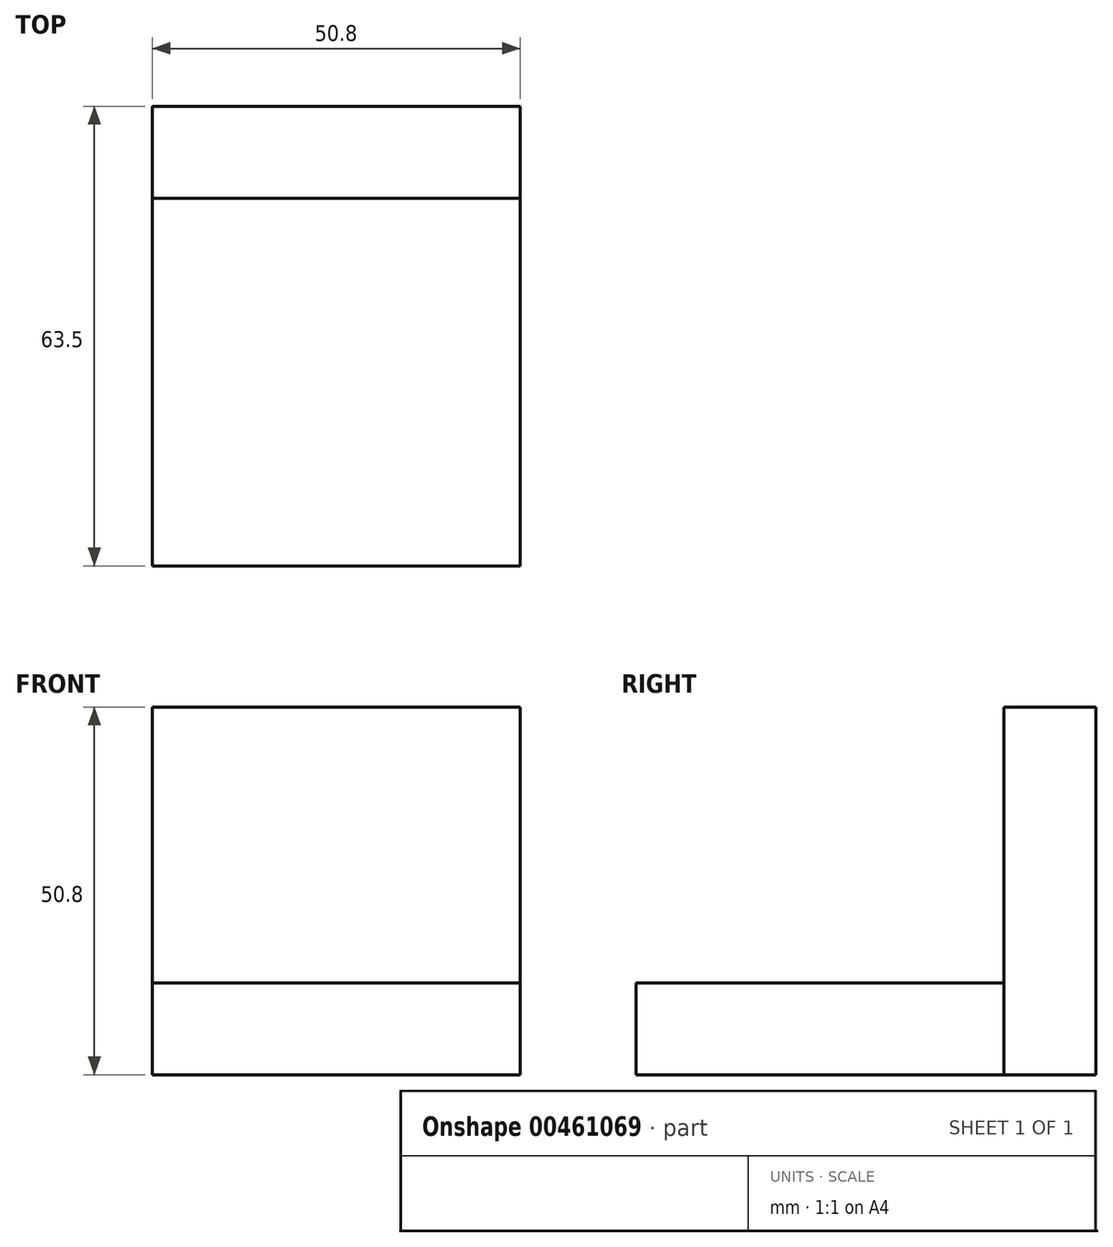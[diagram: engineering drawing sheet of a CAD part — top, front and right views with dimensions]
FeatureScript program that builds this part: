
annotation { "Feature Type Name" : "Feature", "Feature Type Description" : "" }
export const myFeature = defineFeature(function(context is Context, id is Id, definition is map)
    precondition{}
    {
        {
            var Q0;
            Q0=qCreatedBy(makeId("Front.planeOp"),FACE);
            var sketch = newSketch(context, id + "F0", { "sketchPlane" : qUnion([Q0])});
            skLineSegment(sketch, "E0.bottom", {"start": v(-27.86, 37.38) * mm, "end": v(22.94, 37.38) * mm});
            skLineSegment(sketch, "E0.top", {"start": v(-27.86, -13.42) * mm, "end": v(22.94, -13.42) * mm});
            skLineSegment(sketch, "E0.left", {"start": v(-27.86, 37.38) * mm, "end": v(-27.86, -13.42) * mm});
            skLineSegment(sketch, "E0.right", {"start": v(22.94, 37.38) * mm, "end": v(22.94, -13.42) * mm});
            skSolve(sketch);
        }
        {
            var Q0;
            Q0 = qSketchRegion(id + "F0", true);
            extrude(context, id + "F1", {"entities" : qUnion([Q0]), "depth" : 12.7 * mm});
        }
        {
            var Q0;
            Q0=makeQuery(id+"F1.opExtrude","SWEPT_FACE",FACE,{"disambiguationData":[OSD([sQuery(id+"F0.wireOp",EDGE,"E0.top")])]});
            var sketch = newSketch(context, id + "F2", { "sketchPlane" : qUnion([Q0])});
            skLineSegment(sketch, "E1", {"start": v(-27.86, 12.7) * mm, "end": v(-27.86, 63.5) * mm});
            skLineSegment(sketch, "E2", {"start": v(-27.86, 63.5) * mm, "end": v(22.94, 63.5) * mm});
            skLineSegment(sketch, "E3", {"start": v(22.94, 63.5) * mm, "end": v(22.94, 12.7) * mm});
            skSolve(sketch);
        }
        {
            var Q0;
            Q0 = qSketchRegion(id + "F2", true);
            var Q1;
            Q1=makeQuery(id+"F2.imprint","IMPRINT",FACE,{"disambiguationData":[TD([[makeQuery(id+"F2.imprint","IMPRINT",EDGE,{"derivedFrom":sQuery(id+"F2.wireOp",EDGE,"E1")}),-1.0]])]});
            extrude(context, id + "F3", {"entities" : qUnion([Q0, Q1]), "oppositeDirection" : true, "depth" : 12.7 * mm});
        }
        {
            var Q0;
            Q0=makeQuery(id+"F1.opExtrude","CAP_FACE",FACE,{"disambiguationData":[OSD([sQuery(id+"F0.wireOp",EDGE,"E0.bottom"),sQuery(id+"F0.wireOp",EDGE,"E0.top"),sQuery(id+"F0.wireOp",EDGE,"E0.left"),sQuery(id+"F0.wireOp",EDGE,"E0.right")])],"isStart":false});
            var sketch = newSketch(context, id + "F4", { "sketchPlane" : qUnion([Q0])});
            skSolve(sketch);
        }
        {
            var Q0;
            Q0=makeQuery(id+"F4.imprint","IMPRINT",FACE,{"disambiguationData":[TD([[makeQuery(id+"F4.imprint","IMPRINT",EDGE,{"derivedFrom":makeQuery(id+"F1.opExtrude","CAP_EDGE",EDGE,{"disambiguationData":[OSD([sQuery(id+"F0.wireOp",EDGE,"E0.bottom")])],"isStart":false})}),-1.0]])]});
            var sketch = newSketch(context, id + "F5", { "sketchPlane" : qUnion([Q0])});
            skCircle(sketch, "E4", {"center": v(-2.6, 20.1) * mm, "radius": 6.35 * mm});
            skSolve(sketch);
        }
        {
            var Q0;
            Q0=sQuery(id+"F5.wireOp",VERTEX,"E4.center");
            var Q1;
            Q1=makeQuery(id+"F3.opExtrude","SWEPT_BODY",BODY,{"disambiguationData":[OSD([sQuery(id+"F0.wireOp",EDGE,"E0.top"),sQuery(id+"F2.wireOp",EDGE,"E1"),sQuery(id+"F2.wireOp",EDGE,"E2"),sQuery(id+"F2.wireOp",EDGE,"E3")])]});
            hole(context, id + "F6", {"style" : HoleStyle.SIMPLE, "endStyle" : HoleEndStyle.THROUGH, "holeDiameter" : 12.7 * mm, "isTappedThrough" : true, "tappedDepth" : 12.7 * mm, "tapClearance" : 3, "locations" : qUnion([Q0]), "scope" : qUnion([Q1])});
        }
    });
